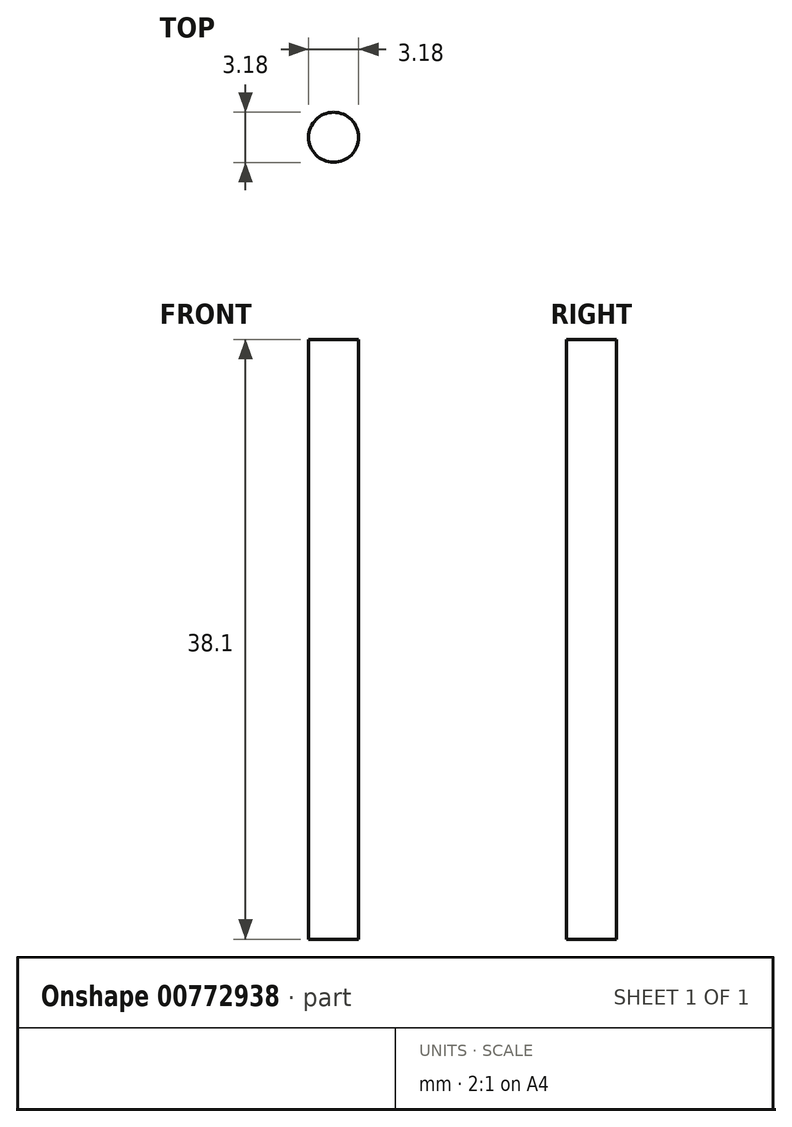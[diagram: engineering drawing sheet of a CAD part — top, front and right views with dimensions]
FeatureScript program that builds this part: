
annotation { "Feature Type Name" : "Feature", "Feature Type Description" : "" }
export const myFeature = defineFeature(function(context is Context, id is Id, definition is map)
    precondition{}
    {
        {
            var Q0;
            Q0=qCreatedBy(makeId("Top.planeOp"),FACE);
            var sketch = newSketch(context, id + "F0", { "sketchPlane" : qUnion([Q0])});
            skCircle(sketch, "E0", {"center": v(0, 0) * mm, "radius": 1.59 * mm});
            skSolve(sketch);
        }
        {
            var Q0;
            Q0=makeQuery(id+"F0.imprint","IMPRINT",FACE,{"disambiguationData":[TD([[makeQuery(id+"F0.imprint","IMPRINT",EDGE,{"derivedFrom":sQuery(id+"F0.wireOp",EDGE,"E0")}),1.0]])]});
            extrude(context, id + "F1", {"entities" : qUnion([Q0]), "depth" : 38.1 * mm, "offsetDistance" : 25.4 * mm});
        }
    });
